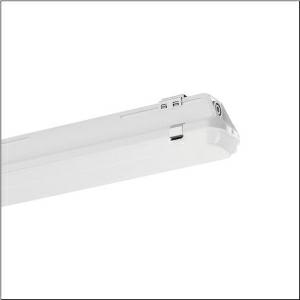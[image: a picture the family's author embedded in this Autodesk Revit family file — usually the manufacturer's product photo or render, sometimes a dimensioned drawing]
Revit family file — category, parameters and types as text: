
# Revit family: monsun_r__21_51fb107p430k_a22f
name_source: partatom
category: Lighting Fixtures
units: mm (PartAtom-declared; Revit-internal decimal feet)

## family parameters
Cut with Voids When Loaded = No
Host = Face
Light Source = No
Part Type = Normal
Room Calculation Point = No
Round Connector Dimension = Use Diameter
Shared = No

## types (1)
- Monsun® 21 (1 x LED, 3940 lm, 22.1 W, 4000K)
    Apparent Load = 22 VA
    CIE Flux Codes = 47 77 93 94 100
    Color Rendering = 80
    Color Temperature = 4000K
    Default Elevation = 1800 mm
    Description = Monsun® 21, damp-proof luminaire, chain hanger, primary optical cover: enclosure, of PMMA, light emission: direct distribution, primary light characteristic: symmetric, installation type: suspended mounting, surface-mounted, horizontal mounting, vertical mounting, LED, rated luminous flux: 3.940lm, luminous efficacy: 178lm/W, light colour: 840, colour temperature: 4000K, control gear: ON/OFF, with terminal, 3-pole, max. 2.5mm², mains connection: 220..240V, AC, 50/60Hz, rated input power: 22W, housing, of glass-fibre reinforced polyester, uncoated, bright grey, incl. chain hanger, length: 1.590mm, width: 90mm, height: 88mm, clip for enclosure, of stainless steel (V2A), ceiling mounting element, of stainless steel (V2A), chain hanger, of stainless steel (V2A), protection rating (complete): IP66, insulation class (complete): insulation class I (protective earthing), certification: CE, ENEC, VDE, UKCA, protection symbol: D, impact resistance: IK04, permissible operating ambient temperature: -25..+35°C, standard: EN 50419, EN 60598-2-1, corresponds to IFS (International Featured Standards) requirements for safety and quality in the food industry, for indoor or canopied outdoor use, no direct snow, no direct sun, no direct rain, LABS conformity tested according to VDMA 24364:2018-05, contact your sales advisor before using the luminaires in applications with unclear chemical exposure, large temperature fluctuations or condensation-forming humidity, packaging unit: 1 piece
    Height = 89 mm
    Lamp = 1 x LED
    Lamp Light Flux = 3940 lm
    Lamp Power = 22.1 W
    Lamp count = 1
    Length = 1590 mm
    Luminous efficacy = 178 lm/W
    Manufacturer = Siteco
    ModVariant = No
    Model = 51FB107P430K
    Mounting Place = Ceiling
    Mounting Type = Surface mounted
    Number of Poles = 1
    OnlyDefault = Yes
    Power Factor = 1
    Product Name = Monsun® 21
    Product group = damp-proof luminaire
    ProductGroupID = 300
    Protection Class = Protection class I
    Protection Degree = IP 66
    RLX_Detail_Level = 1
    RLX_Emergency_Light_Flux = 0 lm
    RLX_Emergency_Type = 0
    RLX_Emergency_Type_DB = No
    RlxData = <blob elided: 88749 chars, md5=b1bc6f09>
    Socket = socket
    Standby Power = 0 W
    System Light Flux = 3940 lm
    System Power = 22 W
    Type Comments = Product without accessories
    Type Image = l_1319656.jpg
    URL = http://relux.com
    VarID = ---
    Voltage = 0 V
    Weight = 0.00 kg
    Width = 90 mm

## geometry (parser evidence)
native form markers: Blend x4, Sweep x13
no freeform markers — native parametric forms only
